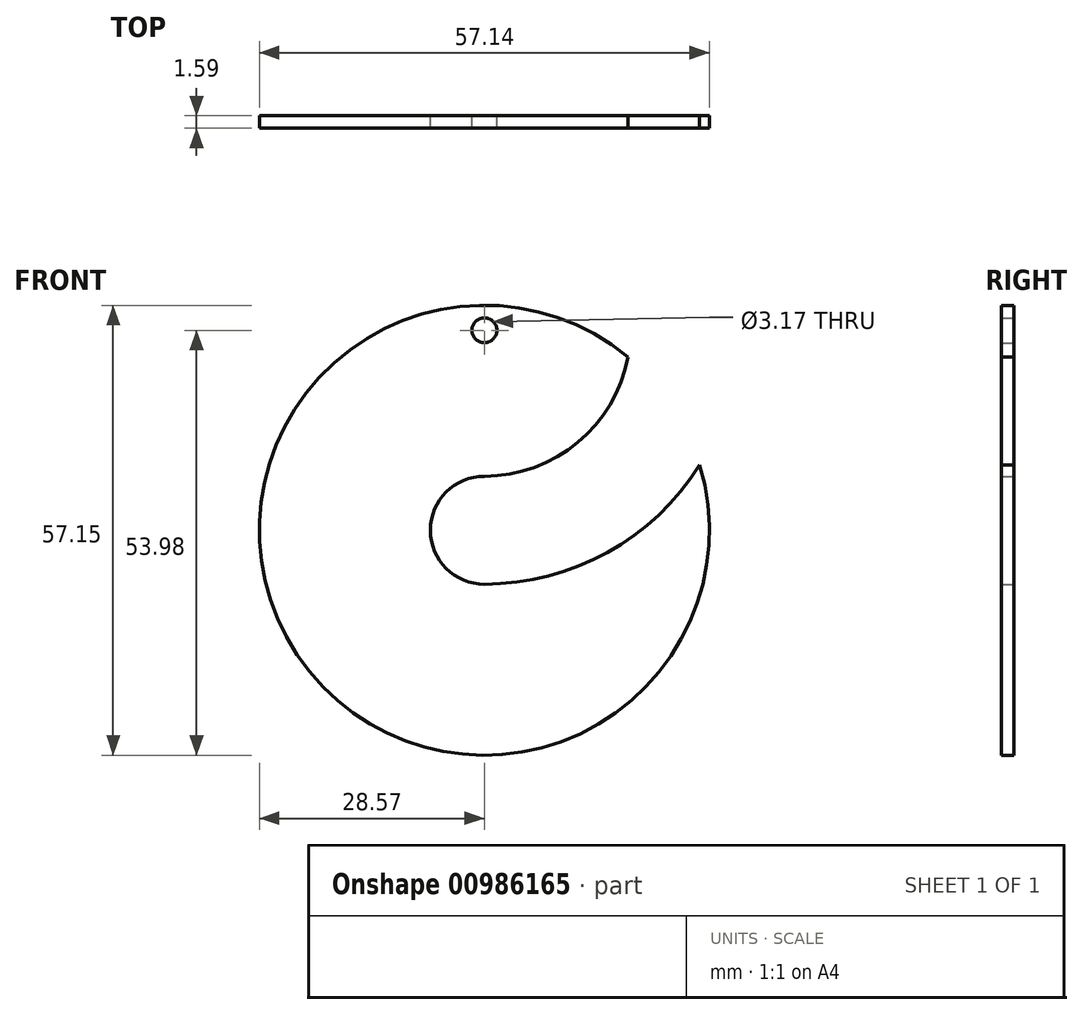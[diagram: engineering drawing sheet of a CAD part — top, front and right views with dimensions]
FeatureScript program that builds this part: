
annotation { "Feature Type Name" : "Feature", "Feature Type Description" : "" }
export const myFeature = defineFeature(function(context is Context, id is Id, definition is map)
    precondition{}
    {
        {
            var Q0;
            Q0=qCreatedBy(makeId("Front.planeOp"),FACE);
            var sketch = newSketch(context, id + "F0", { "sketchPlane" : qUnion([Q0])});
            skArc(sketch, "E0", {"start": v(18.23, 22) * mm, "mid": v(-23.8, -15.82) * mm, "end": v(27.35, 8.29) * mm});
            skArc(sketch, "E1", {"start": v(15.78, 15.66) * mm, "mid": v(-20.16, -9.36) * mm, "end": v(22.14, 1.94) * mm});
            skLineSegment(sketch, "E2", {"start": v(0, 0) * mm, "end": v(0, 28.58) * mm});
            skLineSegment(sketch, "E3", {"start": v(0, 28.58) * mm, "end": v(0, 25.4) * mm});
            skArc(sketch, "E4", {"start": v(0, 6.86) * mm, "mid": v(-6.86, 0) * mm, "end": v(0, -6.86) * mm});
            skArc(sketch, "E5", {"start": v(0, 6.86) * mm, "mid": v(11.85, 11.14) * mm, "end": v(18.23, 22) * mm});
            skArc(sketch, "E6", {"start": v(0, -6.86) * mm, "mid": v(15.63, -2.82) * mm, "end": v(27.35, 8.29) * mm});
            skCircle(sketch, "E7", {"center": v(0, 25.4) * mm, "radius": 1.59 * mm});
            skSolve(sketch);
        }
        {
            var Q0;
            Q0 = qSketchRegion(id + "F0", true);
            extrude(context, id + "F1", {"entities" : qUnion([Q0]), "depth" : 1.59 * mm, "offsetDistance" : 25.4 * mm});
        }
    });
